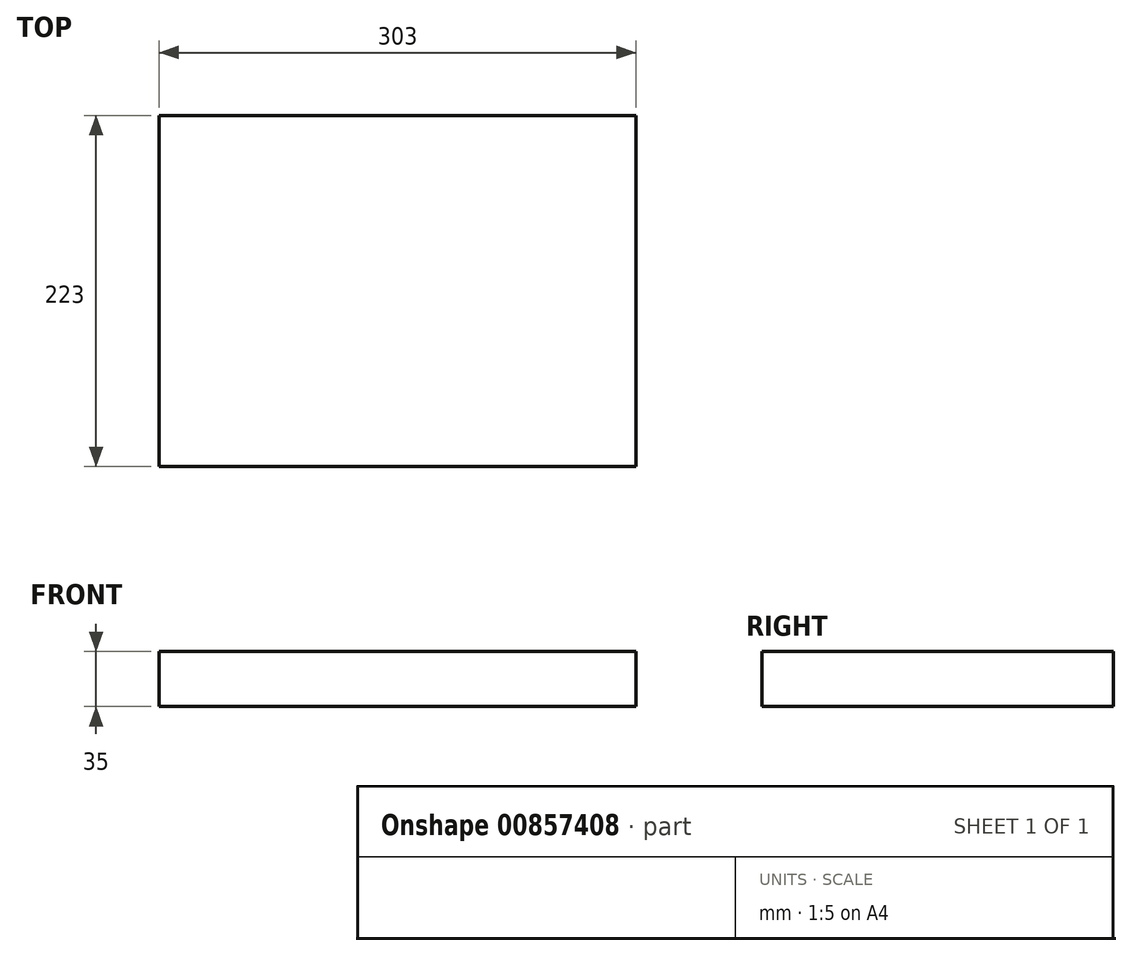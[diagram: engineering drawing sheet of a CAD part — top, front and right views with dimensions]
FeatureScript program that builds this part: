
annotation { "Feature Type Name" : "Feature", "Feature Type Description" : "" }
export const myFeature = defineFeature(function(context is Context, id is Id, definition is map)
    precondition{}
    {
        {
            var Q0;
            Q0=qCreatedBy(makeId("Top.planeOp"),FACE);
            var sketch = newSketch(context, id + "F0", { "sketchPlane" : qUnion([Q0])});
            skLineSegment(sketch, "E0.bottom", {"start": v(151.5, -111.5) * mm, "end": v(-151.5, -111.5) * mm});
            skLineSegment(sketch, "E0.top", {"start": v(151.5, 111.5) * mm, "end": v(-151.5, 111.5) * mm});
            skLineSegment(sketch, "E0.left", {"start": v(151.5, -111.5) * mm, "end": v(151.5, 111.5) * mm});
            skLineSegment(sketch, "E0.right", {"start": v(-151.5, -111.5) * mm, "end": v(-151.5, 111.5) * mm});
            skPoint(sketch, "E0.middle", {"position": v(0, 0) * mm});
            skSolve(sketch);
        }
        {
            var Q0;
            Q0=makeQuery(id+"F0.imprint","IMPRINT",FACE,{"disambiguationData":[TD([[makeQuery(id+"F0.imprint","IMPRINT",EDGE,{"derivedFrom":sQuery(id+"F0.wireOp",EDGE,"E0.bottom")}),-1.0]])]});
            extrude(context, id + "F1", {"entities" : qUnion([Q0]), "depth" : 35 * mm, "offsetDistance" : 25 * mm});
        }
    });
